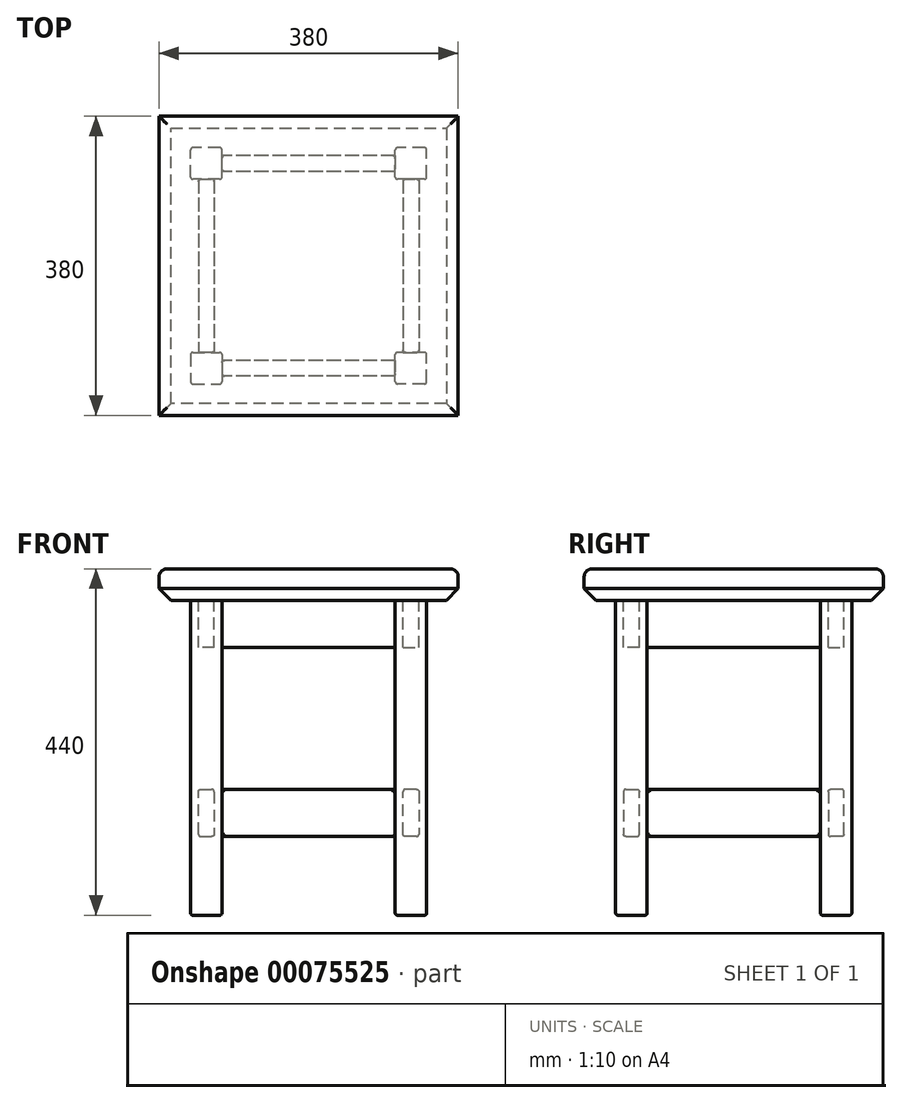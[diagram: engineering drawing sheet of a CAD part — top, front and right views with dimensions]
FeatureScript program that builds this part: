
annotation { "Feature Type Name" : "Feature", "Feature Type Description" : "" }
export const myFeature = defineFeature(function(context is Context, id is Id, definition is map)
    precondition{}
    {
        {
            var Q0;
            Q0=qCreatedBy(makeId("Top.planeOp"),FACE);
            var sketch = newSketch(context, id + "F0", { "sketchPlane" : qUnion([Q0])});
            skLineSegment(sketch, "E0.rect.bottom", {"start": v(-40, 40) * mm, "end": v(0, 40) * mm});
            skLineSegment(sketch, "E0.rect.top", {"start": v(-40, 0) * mm, "end": v(0, 0) * mm});
            skLineSegment(sketch, "E0.rect.left", {"start": v(-40, 40) * mm, "end": v(-40, 0) * mm});
            skLineSegment(sketch, "E0.rect.right", {"start": v(0, 40) * mm, "end": v(0, 0) * mm});
            skPoint(sketch, "E0.rect.middle", {"position": v(-20, 20) * mm});
            skLineSegment(sketch, "E1.rect.bottom", {"start": v(260, 0) * mm, "end": v(220, 0) * mm});
            skLineSegment(sketch, "E1.rect.top", {"start": v(260, 40) * mm, "end": v(220, 40) * mm});
            skLineSegment(sketch, "E1.rect.left", {"start": v(260, 0) * mm, "end": v(260, 40) * mm});
            skLineSegment(sketch, "E1.rect.right", {"start": v(220, 0) * mm, "end": v(220, 40) * mm});
            skPoint(sketch, "E1.rect.middle", {"position": v(240, 20) * mm});
            skLineSegment(sketch, "E2.rect.bottom", {"start": v(0, 260) * mm, "end": v(-40, 260) * mm});
            skLineSegment(sketch, "E2.rect.top", {"start": v(0, 300) * mm, "end": v(-40, 300) * mm});
            skLineSegment(sketch, "E2.rect.left", {"start": v(0, 260) * mm, "end": v(0, 300) * mm});
            skLineSegment(sketch, "E2.rect.right", {"start": v(-40, 260) * mm, "end": v(-40, 300) * mm});
            skPoint(sketch, "E2.rect.middle", {"position": v(-20, 280) * mm});
            skLineSegment(sketch, "E3.rect.bottom", {"start": v(260, 260) * mm, "end": v(220, 260) * mm});
            skLineSegment(sketch, "E3.rect.top", {"start": v(260, 300) * mm, "end": v(220, 300) * mm});
            skLineSegment(sketch, "E3.rect.left", {"start": v(260, 260) * mm, "end": v(260, 300) * mm});
            skLineSegment(sketch, "E3.rect.right", {"start": v(220, 260) * mm, "end": v(220, 300) * mm});
            skPoint(sketch, "E3.rect.middle", {"position": v(240, 280) * mm});
            skSolve(sketch);
        }
        {
            var Q0;
            Q0=makeQuery(id+"F0.imprint","IMPRINT",FACE,{"disambiguationData":[TD([[makeQuery(id+"F0.imprint","IMPRINT",EDGE,{"derivedFrom":sQuery(id+"F0.wireOp",EDGE,"E2.rect.bottom")}),-1.0]])]});
            var Q1;
            Q1=makeQuery(id+"F0.imprint","IMPRINT",FACE,{"disambiguationData":[TD([[makeQuery(id+"F0.imprint","IMPRINT",EDGE,{"derivedFrom":sQuery(id+"F0.wireOp",EDGE,"E0.rect.bottom")}),-1.0]])]});
            var Q2;
            Q2=makeQuery(id+"F0.imprint","IMPRINT",FACE,{"disambiguationData":[TD([[makeQuery(id+"F0.imprint","IMPRINT",EDGE,{"derivedFrom":sQuery(id+"F0.wireOp",EDGE,"E1.rect.bottom")}),-1.0]])]});
            var Q3;
            Q3=makeQuery(id+"F0.imprint","IMPRINT",FACE,{"disambiguationData":[TD([[makeQuery(id+"F0.imprint","IMPRINT",EDGE,{"derivedFrom":sQuery(id+"F0.wireOp",EDGE,"E3.rect.bottom")}),-1.0]])]});
            extrude(context, id + "F1", {"entities" : qUnion([Q0, Q1, Q2, Q3]), "depth" : 400 * mm});
        }
        {
            var Q0;
            Q0=makeQuery(id+"F1.opExtrude","SWEPT_FACE",FACE,{"disambiguationData":[OSD([sQuery(id+"F0.wireOp",EDGE,"E0.rect.right")])]});
            var sketch = newSketch(context, id + "F2", { "sketchPlane" : qUnion([Q0])});
            skLineSegment(sketch, "E4.rect.bottom", {"start": v(30, 100) * mm, "end": v(10, 100) * mm});
            skLineSegment(sketch, "E4.rect.top", {"start": v(30, 160) * mm, "end": v(10, 160) * mm});
            skLineSegment(sketch, "E4.rect.left", {"start": v(30, 100) * mm, "end": v(30, 160) * mm});
            skLineSegment(sketch, "E4.rect.right", {"start": v(10, 100) * mm, "end": v(10, 160) * mm});
            skPoint(sketch, "E4.rect.middle", {"position": v(20, 130) * mm});
            skLineSegment(sketch, "E5.bottom", {"start": v(10, 400) * mm, "end": v(30, 400) * mm});
            skLineSegment(sketch, "E5.top", {"start": v(10, 340) * mm, "end": v(30, 340) * mm});
            skLineSegment(sketch, "E5.left", {"start": v(10, 400) * mm, "end": v(10, 340) * mm});
            skLineSegment(sketch, "E5.right", {"start": v(30, 400) * mm, "end": v(30, 340) * mm});
            skSolve(sketch);
        }
        {
            var Q0;
            Q0 = qSketchRegion(id + "F2", true);
            var Q1;
            Q1=makeQuery(id+"F1.opExtrude","SWEPT_FACE",FACE,{"disambiguationData":[OSD([sQuery(id+"F0.wireOp",EDGE,"E1.rect.right")])]});
            extrude(context, id + "F3", {"entities" : qUnion([Q0]), "endBound" : BoundingType.UP_TO_SURFACE, "endBoundEntityFace" : qUnion([Q1]), "depth" : 25 * mm});
        }
        {
            var Q0;
            Q0=makeQuery(id+"F1.opExtrude","SWEPT_FACE",FACE,{"disambiguationData":[OSD([sQuery(id+"F0.wireOp",EDGE,"E0.rect.top")])]});
            var Q1;
            Q1=makeQuery(id+"F1.opExtrude","SWEPT_FACE",FACE,{"disambiguationData":[OSD([sQuery(id+"F0.wireOp",EDGE,"E0.rect.left")])]});
            cPlane(context, id + "F4", {"entities" : qUnion([Q0, Q1]), "cplaneType" : CPlaneType.MID_PLANE, "offset" : 150 * mm, "width" : 150 * mm, "height" : 150 * mm});
        }
        {
            var Q0;
            Q0=makeQuery(id+"F3.opExtrude","SWEPT_BODY",BODY,{"disambiguationData":[OSD([sQuery(id+"F2.wireOp",EDGE,"E5.bottom"),sQuery(id+"F2.wireOp",EDGE,"E5.top"),sQuery(id+"F2.wireOp",EDGE,"E5.left"),sQuery(id+"F2.wireOp",EDGE,"E5.right")])]});
            var Q1;
            Q1=makeQuery(id+"F3.opExtrude","SWEPT_BODY",BODY,{"disambiguationData":[OSD([sQuery(id+"F2.wireOp",EDGE,"E4.rect.bottom"),sQuery(id+"F2.wireOp",EDGE,"E4.rect.top"),sQuery(id+"F2.wireOp",EDGE,"E4.rect.left"),sQuery(id+"F2.wireOp",EDGE,"E4.rect.right")])]});
            var Q2;
            Q2=qCreatedBy(id+"F4.planeOp",FACE);
            mirror(context, id + "F5", {"entities" : qUnion([Q0, Q1]), "mirrorPlane" : qUnion([Q2])});
        }
        {
            var Q0;
            Q0=makeQuery(id+"F1.opExtrude","SWEPT_FACE",FACE,{"disambiguationData":[OSD([sQuery(id+"F0.wireOp",EDGE,"E2.rect.bottom")])]});
            var Q1;
            Q1=makeQuery(id+"F1.opExtrude","SWEPT_FACE",FACE,{"disambiguationData":[OSD([sQuery(id+"F0.wireOp",EDGE,"E0.rect.bottom")])]});
            cPlane(context, id + "F6", {"entities" : qUnion([Q0, Q1]), "cplaneType" : CPlaneType.MID_PLANE, "offset" : 150 * mm, "width" : 150 * mm, "height" : 150 * mm});
        }
        {
            var Q0;
            Q0=makeQuery(id+"F3.opExtrude","SWEPT_BODY",BODY,{"disambiguationData":[OSD([sQuery(id+"F2.wireOp",EDGE,"E5.bottom"),sQuery(id+"F2.wireOp",EDGE,"E5.top"),sQuery(id+"F2.wireOp",EDGE,"E5.left"),sQuery(id+"F2.wireOp",EDGE,"E5.right")])]});
            var Q1;
            Q1=makeQuery(id+"F3.opExtrude","SWEPT_BODY",BODY,{"disambiguationData":[OSD([sQuery(id+"F2.wireOp",EDGE,"E4.rect.bottom"),sQuery(id+"F2.wireOp",EDGE,"E4.rect.top"),sQuery(id+"F2.wireOp",EDGE,"E4.rect.left"),sQuery(id+"F2.wireOp",EDGE,"E4.rect.right")])]});
            var Q2;
            Q2=qCreatedBy(id+"F6.planeOp",FACE);
            mirror(context, id + "F7", {"entities" : qUnion([Q0, Q1]), "mirrorPlane" : qUnion([Q2])});
        }
        {
            var Q0;
            Q0=makeQuery(id+"F1.opExtrude","SWEPT_FACE",FACE,{"disambiguationData":[OSD([sQuery(id+"F0.wireOp",EDGE,"E1.rect.right")])]});
            var Q1;
            Q1=makeQuery(id+"F1.opExtrude","SWEPT_FACE",FACE,{"disambiguationData":[OSD([sQuery(id+"F0.wireOp",EDGE,"E0.rect.right")])]});
            cPlane(context, id + "F8", {"entities" : qUnion([Q0, Q1]), "cplaneType" : CPlaneType.MID_PLANE, "offset" : 150 * mm, "width" : 150 * mm, "height" : 150 * mm});
        }
        {
            var Q0;
            Q0=makeQuery(id+"F5.opPattern","COPY",BODY,{"derivedFrom":makeQuery(id+"F3.opExtrude","SWEPT_BODY",BODY,{"disambiguationData":[OSD([sQuery(id+"F2.wireOp",EDGE,"E5.bottom"),sQuery(id+"F2.wireOp",EDGE,"E5.top"),sQuery(id+"F2.wireOp",EDGE,"E5.left"),sQuery(id+"F2.wireOp",EDGE,"E5.right")])]}),"instanceName":"1"});
            var Q1;
            Q1=makeQuery(id+"F5.opPattern","COPY",BODY,{"derivedFrom":makeQuery(id+"F3.opExtrude","SWEPT_BODY",BODY,{"disambiguationData":[OSD([sQuery(id+"F2.wireOp",EDGE,"E4.rect.bottom"),sQuery(id+"F2.wireOp",EDGE,"E4.rect.top"),sQuery(id+"F2.wireOp",EDGE,"E4.rect.left"),sQuery(id+"F2.wireOp",EDGE,"E4.rect.right")])]}),"instanceName":"1"});
            var Q2;
            Q2=qCreatedBy(id+"F8.planeOp",FACE);
            mirror(context, id + "F9", {"entities" : qUnion([Q0, Q1]), "mirrorPlane" : qUnion([Q2])});
        }
        {
            var Q0;
            Q0=makeQuery(id+"F1.opExtrude","CAP_FACE",FACE,{"disambiguationData":[OSD([sQuery(id+"F0.wireOp",EDGE,"E2.rect.bottom"),sQuery(id+"F0.wireOp",EDGE,"E2.rect.top"),sQuery(id+"F0.wireOp",EDGE,"E2.rect.left"),sQuery(id+"F0.wireOp",EDGE,"E2.rect.right")])],"isStart":false});
            var sketch = newSketch(context, id + "F10", { "sketchPlane" : qUnion([Q0])});
            skLineSegment(sketch, "E6.bottom", {"start": v(-80, 340) * mm, "end": v(300, 340) * mm});
            skLineSegment(sketch, "E6.top", {"start": v(-80, -40) * mm, "end": v(300, -40) * mm});
            skLineSegment(sketch, "E6.left", {"start": v(-80, 340) * mm, "end": v(-80, -40) * mm});
            skLineSegment(sketch, "E6.right", {"start": v(300, 340) * mm, "end": v(300, -40) * mm});
            skSolve(sketch);
        }
        {
            var Q0;
            Q0 = qSketchRegion(id + "F10", true);
            extrude(context, id + "F11", {"entities" : qUnion([Q0]), "depth" : 40 * mm});
        }
        {
            var Q0;
            Q0=makeQuery(id+"F11.opExtrude","CAP_FACE",FACE,{"disambiguationData":[OSD([sQuery(id+"F10.wireOp",EDGE,"E6.bottom"),sQuery(id+"F10.wireOp",EDGE,"E6.top"),sQuery(id+"F10.wireOp",EDGE,"E6.left"),sQuery(id+"F10.wireOp",EDGE,"E6.right")])],"isStart":false});
            fillet(context, id + "F12", {"entities" : qUnion([Q0]), "radius" : 10 * mm, "tangentPropagation" : true, "allowEdgeOverflow" : false});
        }
        {
            var Q0;
            Q0=makeQuery(id+"F11.opExtrude","CAP_FACE",FACE,{"disambiguationData":[OSD([sQuery(id+"F10.wireOp",EDGE,"E6.bottom"),sQuery(id+"F10.wireOp",EDGE,"E6.top"),sQuery(id+"F10.wireOp",EDGE,"E6.left"),sQuery(id+"F10.wireOp",EDGE,"E6.right")])],"isStart":true});
            chamfer(context, id + "F13", {"entities" : qUnion([Q0]), "width" : 15 * mm, "tangentPropagation" : true});
        }
        {
            var Q0;
            Q0=makeQuery(id+"F1.opExtrude","SWEPT_FACE",FACE,{"disambiguationData":[OSD([sQuery(id+"F0.wireOp",EDGE,"E0.rect.top")])]});
            var Q1;
            Q1=makeQuery(id+"F1.opExtrude","SWEPT_FACE",FACE,{"disambiguationData":[OSD([sQuery(id+"F0.wireOp",EDGE,"E0.rect.left")])]});
            var Q2;
            Q2=makeQuery(id+"F1.opExtrude","SWEPT_FACE",FACE,{"disambiguationData":[OSD([sQuery(id+"F0.wireOp",EDGE,"E0.rect.bottom")])]});
            var Q3;
            Q3=makeQuery(id+"F1.opExtrude","SWEPT_FACE",FACE,{"disambiguationData":[OSD([sQuery(id+"F0.wireOp",EDGE,"E0.rect.right")])]});
            var Q4;
            Q4=makeQuery(id+"F1.opExtrude","SWEPT_FACE",FACE,{"disambiguationData":[OSD([sQuery(id+"F0.wireOp",EDGE,"E1.rect.left")])]});
            var Q5;
            Q5=makeQuery(id+"F1.opExtrude","SWEPT_FACE",FACE,{"disambiguationData":[OSD([sQuery(id+"F0.wireOp",EDGE,"E1.rect.top")])]});
            var Q6;
            Q6=makeQuery(id+"F1.opExtrude","SWEPT_FACE",FACE,{"disambiguationData":[OSD([sQuery(id+"F0.wireOp",EDGE,"E1.rect.bottom")])]});
            var Q7;
            Q7=makeQuery(id+"F1.opExtrude","SWEPT_FACE",FACE,{"disambiguationData":[OSD([sQuery(id+"F0.wireOp",EDGE,"E1.rect.right")])]});
            var Q8;
            Q8=makeQuery(id+"F3.opExtrude","SWEPT_FACE",FACE,{"disambiguationData":[OSD([sQuery(id+"F2.wireOp",EDGE,"E4.rect.right")])]});
            var Q9;
            Q9=makeQuery(id+"F5.opPattern","COPY",FACE,{"derivedFrom":makeQuery(id+"F3.opExtrude","SWEPT_FACE",FACE,{"disambiguationData":[OSD([sQuery(id+"F2.wireOp",EDGE,"E4.rect.right")])]}),"instanceName":"1"});
            var Q10;
            Q10=makeQuery(id+"F9.opPattern","COPY",FACE,{"derivedFrom":makeQuery(id+"F5.opPattern","COPY",FACE,{"derivedFrom":makeQuery(id+"F3.opExtrude","SWEPT_FACE",FACE,{"disambiguationData":[OSD([sQuery(id+"F2.wireOp",EDGE,"E4.rect.right")])]}),"instanceName":"1"}),"instanceName":"1"});
            var Q11;
            Q11=makeQuery(id+"F7.opPattern","COPY",FACE,{"derivedFrom":makeQuery(id+"F3.opExtrude","SWEPT_FACE",FACE,{"disambiguationData":[OSD([sQuery(id+"F2.wireOp",EDGE,"E4.rect.right")])]}),"instanceName":"1"});
            var Q12;
            Q12=makeQuery(id+"F1.opExtrude","SWEPT_FACE",FACE,{"disambiguationData":[OSD([sQuery(id+"F0.wireOp",EDGE,"E3.rect.top")])]});
            var Q13;
            Q13=makeQuery(id+"F1.opExtrude","SWEPT_FACE",FACE,{"disambiguationData":[OSD([sQuery(id+"F0.wireOp",EDGE,"E3.rect.left")])]});
            var Q14;
            Q14=makeQuery(id+"F1.opExtrude","SWEPT_FACE",FACE,{"disambiguationData":[OSD([sQuery(id+"F0.wireOp",EDGE,"E3.rect.bottom")])]});
            var Q15;
            Q15=makeQuery(id+"F7.opPattern","COPY",FACE,{"derivedFrom":makeQuery(id+"F3.opExtrude","SWEPT_FACE",FACE,{"disambiguationData":[OSD([sQuery(id+"F2.wireOp",EDGE,"E4.rect.left")])]}),"instanceName":"1"});
            var Q16;
            Q16=makeQuery(id+"F5.opPattern","COPY",FACE,{"derivedFrom":makeQuery(id+"F3.opExtrude","SWEPT_FACE",FACE,{"disambiguationData":[OSD([sQuery(id+"F2.wireOp",EDGE,"E4.rect.left")])]}),"instanceName":"1"});
            var Q17;
            Q17=makeQuery(id+"F1.opExtrude","SWEPT_FACE",FACE,{"disambiguationData":[OSD([sQuery(id+"F0.wireOp",EDGE,"E3.rect.right")])]});
            var Q18;
            Q18=makeQuery(id+"F9.opPattern","COPY",FACE,{"derivedFrom":makeQuery(id+"F5.opPattern","COPY",FACE,{"derivedFrom":makeQuery(id+"F3.opExtrude","SWEPT_FACE",FACE,{"disambiguationData":[OSD([sQuery(id+"F2.wireOp",EDGE,"E4.rect.left")])]}),"instanceName":"1"}),"instanceName":"1"});
            var Q19;
            Q19=makeQuery(id+"F1.opExtrude","SWEPT_FACE",FACE,{"disambiguationData":[OSD([sQuery(id+"F0.wireOp",EDGE,"E2.rect.bottom")])]});
            var Q20;
            Q20=makeQuery(id+"F1.opExtrude","SWEPT_FACE",FACE,{"disambiguationData":[OSD([sQuery(id+"F0.wireOp",EDGE,"E2.rect.right")])]});
            var Q21;
            Q21=makeQuery(id+"F3.opExtrude","SWEPT_FACE",FACE,{"disambiguationData":[OSD([sQuery(id+"F2.wireOp",EDGE,"E4.rect.left")])]});
            var Q22;
            Q22=makeQuery(id+"F1.opExtrude","SWEPT_FACE",FACE,{"disambiguationData":[OSD([sQuery(id+"F0.wireOp",EDGE,"E2.rect.top")])]});
            var Q23;
            Q23=makeQuery(id+"F1.opExtrude","SWEPT_FACE",FACE,{"disambiguationData":[OSD([sQuery(id+"F0.wireOp",EDGE,"E2.rect.left")])]});
            fillet(context, id + "F14", {"entities" : qUnion([Q0, Q1, Q2, Q3, Q4, Q5, Q6, Q7, Q8, Q9, Q10, Q11, Q12, Q13, Q14, Q15, Q16, Q17, Q18, Q19, Q20, Q21, Q22, Q23]), "radius" : 3 * mm, "tangentPropagation" : true, "allowEdgeOverflow" : false});
        }
    });
